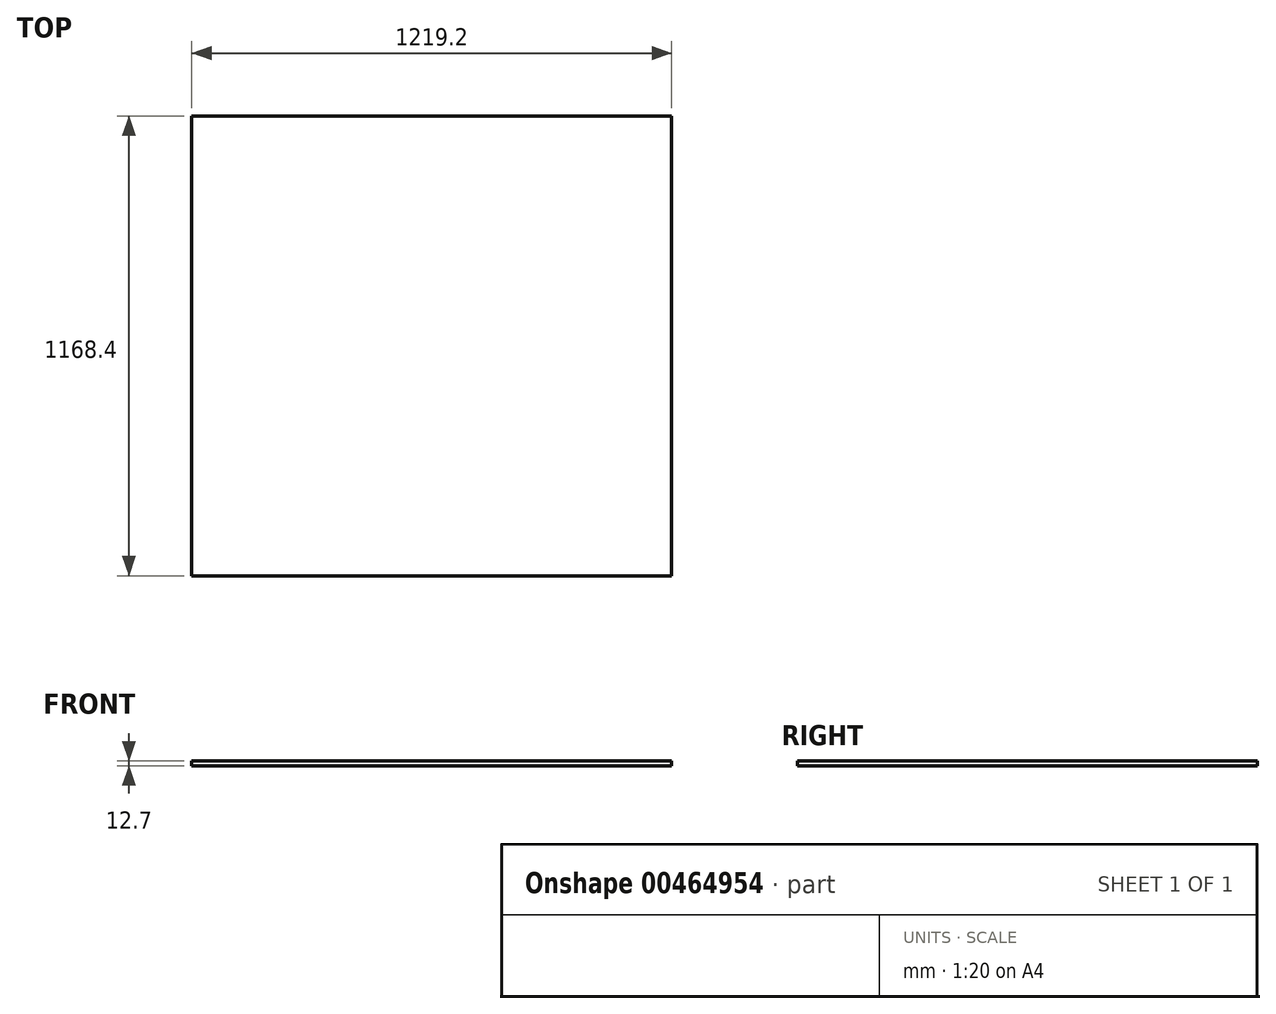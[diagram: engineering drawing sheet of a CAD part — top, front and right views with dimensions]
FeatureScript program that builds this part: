
annotation { "Feature Type Name" : "Feature", "Feature Type Description" : "" }
export const myFeature = defineFeature(function(context is Context, id is Id, definition is map)
    precondition{}
    {
        {
            var Q0;
            Q0=qCreatedBy(makeId("Top.planeOp"),FACE);
            var sketch = newSketch(context, id + "F0", { "sketchPlane" : qUnion([Q0])});
            skLineSegment(sketch, "E0.bottom", {"start": v(-609.6, -584.2) * mm, "end": v(609.6, -584.2) * mm});
            skLineSegment(sketch, "E0.top", {"start": v(-609.6, 584.2) * mm, "end": v(609.6, 584.2) * mm});
            skLineSegment(sketch, "E0.left", {"start": v(-609.6, -584.2) * mm, "end": v(-609.6, 584.2) * mm});
            skLineSegment(sketch, "E0.right", {"start": v(609.6, -584.2) * mm, "end": v(609.6, 584.2) * mm});
            skPoint(sketch, "E0.middle", {"position": v(0, 0) * mm});
            skSolve(sketch);
        }
        {
            var Q0;
            Q0 = qSketchRegion(id + "F0", true);
            extrude(context, id + "F1", {"entities" : qUnion([Q0]), "depth" : 12.7 * mm});
        }
    });
